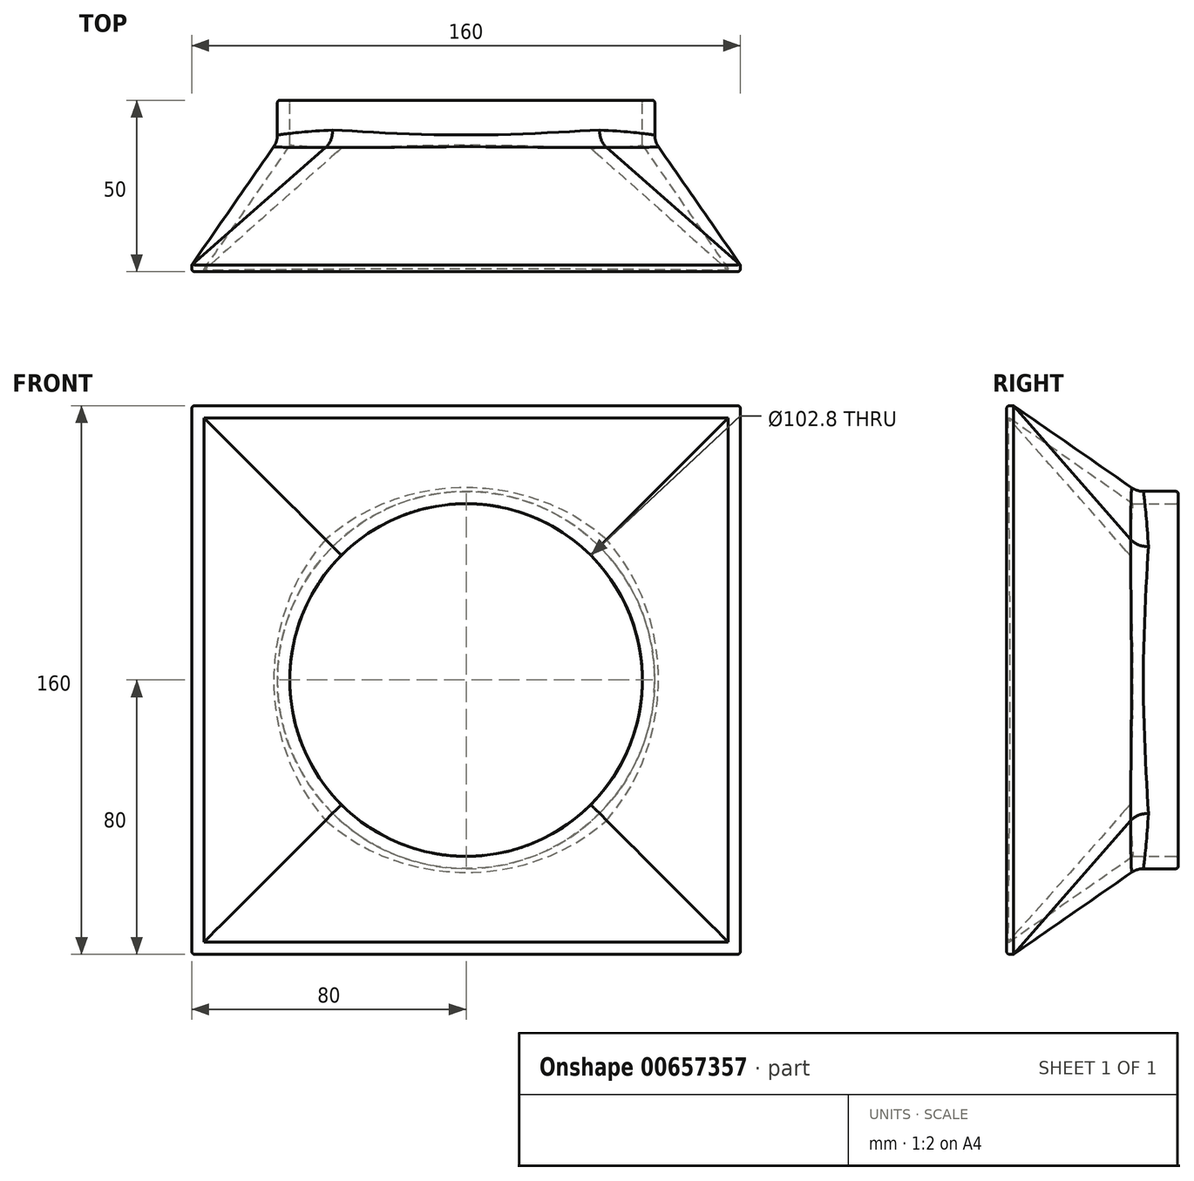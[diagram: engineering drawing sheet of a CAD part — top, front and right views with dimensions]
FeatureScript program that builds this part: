
annotation { "Feature Type Name" : "Feature", "Feature Type Description" : "" }
export const myFeature = defineFeature(function(context is Context, id is Id, definition is map)
    precondition{}
    {
        {
            var Q0;
            Q0=qCreatedBy(makeId("Front.planeOp"),FACE);
            var sketch = newSketch(context, id + "F0", { "sketchPlane" : qUnion([Q0])});
            skCircle(sketch, "E0", {"center": v(0, 0) * mm, "radius": 55 * mm});
            skSolve(sketch);
        }
        {
            var Q0;
            Q0 = qSketchRegion(id + "F0", true);
            extrude(context, id + "F1", {"entities" : qUnion([Q0]), "depth" : 12 * mm, "offsetDistance" : 25 * mm});
        }
        {
            var Q0;
            Q0=qCreatedBy(makeId("Front.planeOp"),FACE);
            cPlane(context, id + "F2", {"entities" : qUnion([Q0]), "cplaneType" : CPlaneType.OFFSET, "offset" : 48 * mm, "width" : 150 * mm, "height" : 150 * mm});
        }
        {
            var Q0;
            Q0=qCreatedBy(id+"F2.planeOp",FACE);
            var sketch = newSketch(context, id + "F3", { "sketchPlane" : qUnion([Q0])});
            skPoint(sketch, "E1.middle", {"position": v(0, 0) * mm});
            skLineSegment(sketch, "E2.bottom", {"start": v(80, 80) * mm, "end": v(-80, 80) * mm});
            skLineSegment(sketch, "E2.top", {"start": v(80, -80) * mm, "end": v(-80, -80) * mm});
            skLineSegment(sketch, "E2.left", {"start": v(80, 80) * mm, "end": v(80, -80) * mm});
            skLineSegment(sketch, "E2.right", {"start": v(-80, 80) * mm, "end": v(-80, -80) * mm});
            skPoint(sketch, "E1.top.end.orphan", {"position": v(-76.6, -76.6) * mm});
            skPoint(sketch, "E1.left.end.orphan", {"position": v(76.6, -76.6) * mm});
            skPoint(sketch, "E1.bottom.end.orphan", {"position": v(-76.6, 76.6) * mm});
            skPoint(sketch, "E1.bottom.start.orphan", {"position": v(76.6, 76.6) * mm});
            skSolve(sketch);
        }
        {
            var Q0;
            Q0 = qSketchRegion(id + "F3", true);
            extrude(context, id + "F4", {"entities" : qUnion([Q0]), "flatOperationType" : FlatOperationType.REMOVE, "depth" : 2 * mm, "offsetDistance" : 25 * mm, "domain" : OperationDomain.MODEL});
        }
        {
            var Q1;
            Q1=makeQuery(id+"F4.opExtrude","CAP_FACE",FACE,{"disambiguationData":[OSD([sQuery(id+"F3.wireOp",EDGE,"E2.bottom"),sQuery(id+"F3.wireOp",EDGE,"E2.top"),sQuery(id+"F3.wireOp",EDGE,"E2.left"),sQuery(id+"F3.wireOp",EDGE,"E2.right")])],"isStart":true});
            var Q2;
            Q2=makeQuery(id+"F1.opExtrude","CAP_FACE",FACE,{"disambiguationData":[OSD([sQuery(id+"F0.wireOp",EDGE,"E0")])],"isStart":false});
            loft(context, id + "F5", {"operationType" : NewBodyOperationType.ADD, "sheetProfilesArray" : [{ "sheetProfileEntities" : qUnion([Q1]) }, { "sheetProfileEntities" : qUnion([Q2]) }]});
        }
        {
            var Q0;
            Q0=makeQuery(id+"F4.opExtrude","CAP_FACE",FACE,{"disambiguationData":[OSD([sQuery(id+"F3.wireOp",EDGE,"E2.bottom"),sQuery(id+"F3.wireOp",EDGE,"E2.top"),sQuery(id+"F3.wireOp",EDGE,"E2.left"),sQuery(id+"F3.wireOp",EDGE,"E2.right")])],"isStart":false});
            var Q1;
            Q1=makeQuery(id+"F1.opExtrude","CAP_FACE",FACE,{"disambiguationData":[OSD([sQuery(id+"F0.wireOp",EDGE,"E0")])],"isStart":true});
            shell(context, id + "F6", {"entities" : qUnion([Q0, Q1]), "thickness" : 3.6 * mm});
        }
        {
            var Q0;
            Q0=makeQuery(id+"F4.opExtrude","CAP_EDGE",EDGE,{"disambiguationData":[OSD([sQuery(id+"F3.wireOp",EDGE,"E2.left")])],"isStart":false});
            var Q1;
            Q1=makeQuery(id+"F4.opExtrude","CAP_EDGE",EDGE,{"disambiguationData":[OSD([sQuery(id+"F3.wireOp",EDGE,"E2.bottom")])],"isStart":false});
            var Q2;
            Q2=makeQuery(id+"F4.opExtrude","CAP_EDGE",EDGE,{"disambiguationData":[OSD([sQuery(id+"F3.wireOp",EDGE,"E2.top")])],"isStart":false});
            var Q3;
            Q3=makeQuery(id+"F4.opExtrude","SWEPT_EDGE",EDGE,{"disambiguationData":[OSD([sQuery(id+"F3.wireOp",EDGE,"E2.top"),sQuery(id+"F3.wireOp",EDGE,"E2.right")])]});
            var Q4;
            Q4=makeQuery(id+"F4.opExtrude","CAP_EDGE",EDGE,{"disambiguationData":[OSD([sQuery(id+"F3.wireOp",EDGE,"E2.right")])],"isStart":false});
            var Q5;
            Q5=makeQuery(id+"F4.opExtrude","SWEPT_EDGE",EDGE,{"disambiguationData":[OSD([sQuery(id+"F3.wireOp",EDGE,"E2.bottom"),sQuery(id+"F3.wireOp",EDGE,"E2.right")])]});
            var Q6;
            Q6=makeQuery(id+"F4.opExtrude","SWEPT_EDGE",EDGE,{"disambiguationData":[OSD([sQuery(id+"F3.wireOp",EDGE,"E2.bottom"),sQuery(id+"F3.wireOp",EDGE,"E2.left")])]});
            var Q7;
            Q7=makeQuery(id+"F4.opExtrude","SWEPT_EDGE",EDGE,{"disambiguationData":[OSD([sQuery(id+"F3.wireOp",EDGE,"E2.top"),sQuery(id+"F3.wireOp",EDGE,"E2.left")])]});
            fillet(context, id + "F7", {"entities" : qUnion([Q0, Q1, Q2, Q3, Q4, Q5, Q6, Q7]), "radius" : 1 * mm, "tangentPropagation" : true, "allowEdgeOverflow" : false});
        }
        {
            var Q0;
            Q0=makeQuery(id+"F1.opExtrude","CAP_FACE",FACE,{"disambiguationData":[OSD([sQuery(id+"F0.wireOp",EDGE,"E0")])],"isStart":true});
            fillet(context, id + "F8", {"entities" : qUnion([Q0]), "radius" : .7 * mm, "tangentPropagation" : true, "allowEdgeOverflow" : false});
        }
        {
            var Q0;
            {var subQ0=sQuery(id+"F0.wireOp",EDGE,"E0");Q0=makeQuery(id+"F5.boolean.opBoolean","MERGE",EDGE,{"derivedFrom":[makeQuery(id+"F1.opExtrude","CAP_EDGE",EDGE,{"disambiguationData":[OSD([subQ0])],"isStart":false}),makeQuery(id+"F5.opLoft","MID_CAP_EDGE",EDGE,{"disambiguationData":[OSD([subQ0,sQuery(id+"F3.wireOp",EDGE,"E2.bottom"),sQuery(id+"F3.wireOp",EDGE,"E2.top"),sQuery(id+"F3.wireOp",EDGE,"E2.left"),sQuery(id+"F3.wireOp",EDGE,"E2.right")])],"capPos":1.0})]});}
            var Q1;
            {var subQ0=sQuery(id+"F0.wireOp",EDGE,"E0");Q1=makeQuery(id+"F5.boolean.opBoolean","MERGE",EDGE,{"derivedFrom":[makeQuery(id+"F1.opExtrude","CAP_EDGE",EDGE,{"disambiguationData":[OSD([subQ0])],"isStart":false}),makeQuery(id+"F5.opLoft","MID_CAP_EDGE",EDGE,{"disambiguationData":[OSD([subQ0,sQuery(id+"F3.wireOp",EDGE,"E2.top"),sQuery(id+"F3.wireOp",EDGE,"E2.left"),sQuery(id+"F3.wireOp",EDGE,"E2.right")])],"capPos":1.0})]});}
            var Q2;
            {var subQ0=sQuery(id+"F0.wireOp",EDGE,"E0");Q2=makeQuery(id+"F5.boolean.opBoolean","MERGE",EDGE,{"derivedFrom":[makeQuery(id+"F1.opExtrude","CAP_EDGE",EDGE,{"disambiguationData":[OSD([subQ0])],"isStart":false}),makeQuery(id+"F5.opLoft","MID_CAP_EDGE",EDGE,{"disambiguationData":[OSD([subQ0,sQuery(id+"F3.wireOp",EDGE,"E2.bottom"),sQuery(id+"F3.wireOp",EDGE,"E2.top"),sQuery(id+"F3.wireOp",EDGE,"E2.left")])],"capPos":1.0})]});}
            var Q3;
            {var subQ0=sQuery(id+"F0.wireOp",EDGE,"E0");Q3=makeQuery(id+"F5.boolean.opBoolean","MERGE",EDGE,{"derivedFrom":[makeQuery(id+"F1.opExtrude","CAP_EDGE",EDGE,{"disambiguationData":[OSD([subQ0])],"isStart":false}),makeQuery(id+"F5.opLoft","MID_CAP_EDGE",EDGE,{"disambiguationData":[OSD([subQ0,sQuery(id+"F3.wireOp",EDGE,"E2.bottom"),sQuery(id+"F3.wireOp",EDGE,"E2.left")])],"capPos":1.0})]});}
            fillet(context, id + "F9", {"entities" : qUnion([Q0, Q1, Q2, Q3]), "radius" : 6 * mm, "tangentPropagation" : true, "allowEdgeOverflow" : false});
        }
    });
